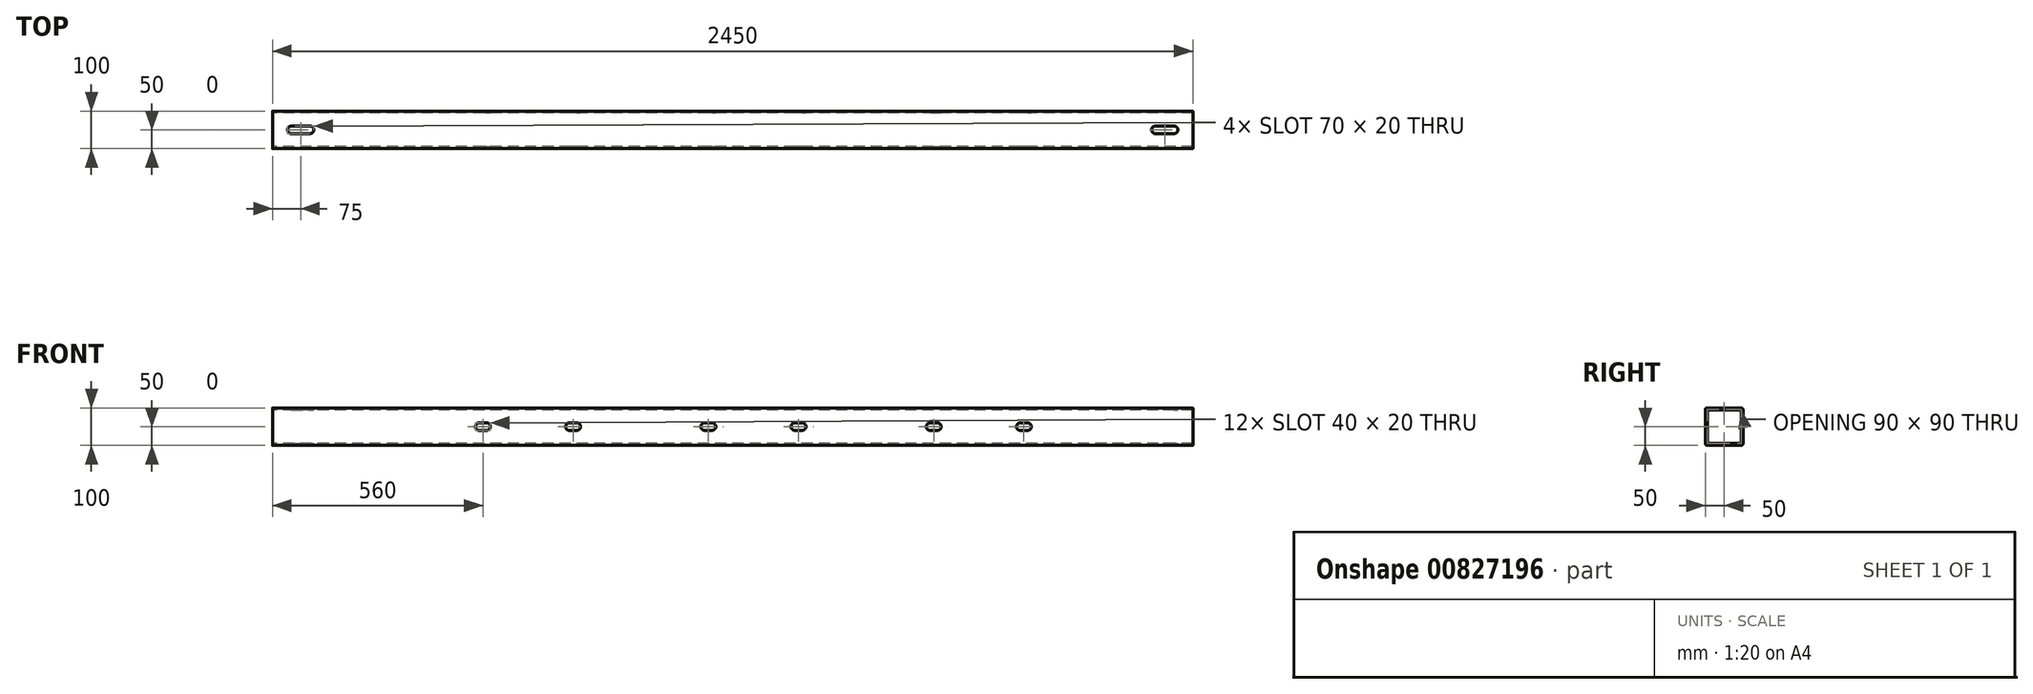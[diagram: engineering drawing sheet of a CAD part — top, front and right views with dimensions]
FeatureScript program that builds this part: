
annotation { "Feature Type Name" : "Feature", "Feature Type Description" : "" }
export const myFeature = defineFeature(function(context is Context, id is Id, definition is map)
    precondition{}
    {
        {
            var Q0;
            Q0=qCreatedBy(makeId("Right.planeOp"),FACE);
            var sketch = newSketch(context, id + "F0", { "sketchPlane" : qUnion([Q0])});
            skLineSegment(sketch, "E0.bottom", {"start": v(-45, 50) * mm, "end": v(45, 50) * mm});
            skLineSegment(sketch, "E0.top", {"start": v(-45, -50) * mm, "end": v(45, -50) * mm});
            skLineSegment(sketch, "E0.left", {"start": v(-50, 45) * mm, "end": v(-50, -45) * mm});
            skLineSegment(sketch, "E0.right", {"start": v(50, 45) * mm, "end": v(50, -45) * mm});
            skLineSegment(sketch, "E1.bottom", {"start": v(-41, 45) * mm, "end": v(41, 45) * mm});
            skLineSegment(sketch, "E1.top", {"start": v(-41, -45) * mm, "end": v(41, -45) * mm});
            skLineSegment(sketch, "E1.left", {"start": v(-45, 41) * mm, "end": v(-45, -41) * mm});
            skLineSegment(sketch, "E1.right", {"start": v(45, 41) * mm, "end": v(45, -41) * mm});
            skPoint(sketch, "E2.visualSharp", {"position": v(-45, 45) * mm});
            skArc(sketch, "E2.filletArc", {"start": v(-41, 45) * mm, "mid": v(-43.83, 43.83) * mm, "end": v(-45, 41) * mm});
            skPoint(sketch, "E3.visualSharp", {"position": v(-45, -45) * mm});
            skArc(sketch, "E3.filletArc", {"start": v(-45, -41) * mm, "mid": v(-43.83, -43.83) * mm, "end": v(-41, -45) * mm});
            skPoint(sketch, "E4.visualSharp", {"position": v(45, -45) * mm});
            skArc(sketch, "E4.filletArc", {"start": v(41, -45) * mm, "mid": v(43.83, -43.83) * mm, "end": v(45, -41) * mm});
            skPoint(sketch, "E5.visualSharp", {"position": v(45, 45) * mm});
            skArc(sketch, "E5.filletArc", {"start": v(45, 41) * mm, "mid": v(43.83, 43.83) * mm, "end": v(41, 45) * mm});
            skPoint(sketch, "E6.visualSharp", {"position": v(-50, 50) * mm});
            skArc(sketch, "E6.filletArc", {"start": v(-45, 50) * mm, "mid": v(-48.54, 48.54) * mm, "end": v(-50, 45) * mm});
            skPoint(sketch, "E7.visualSharp", {"position": v(-50, -50) * mm});
            skArc(sketch, "E7.filletArc", {"start": v(-50, -45) * mm, "mid": v(-48.54, -48.54) * mm, "end": v(-45, -50) * mm});
            skPoint(sketch, "E8.visualSharp", {"position": v(50, -50) * mm});
            skArc(sketch, "E8.filletArc", {"start": v(45, -50) * mm, "mid": v(48.54, -48.54) * mm, "end": v(50, -45) * mm});
            skPoint(sketch, "E9.visualSharp", {"position": v(50, 50) * mm});
            skArc(sketch, "E9.filletArc", {"start": v(50, 45) * mm, "mid": v(48.54, 48.54) * mm, "end": v(45, 50) * mm});
            skSolve(sketch);
        }
        {
            var Q0;
            Q0=makeQuery(id+"F0.imprint","IMPRINT",FACE,{"disambiguationData":[TD([[makeQuery(id+"F0.imprint","IMPRINT",EDGE,{"derivedFrom":sQuery(id+"F0.wireOp",EDGE,"E0.bottom")}),-1.0]])]});
            extrude(context, id + "F1", {"entities" : qUnion([Q0]), "endBound" : BoundingType.SYMMETRIC, "depth" : 2450 * mm, "offsetDistance" : 25 * mm});
        }
        {
            var Q0;
            Q0=makeQuery(id+"F1.opExtrude","SWEPT_FACE",FACE,{"disambiguationData":[OSD([sQuery(id+"F0.wireOp",EDGE,"E0.left")])]});
            var sketch = newSketch(context, id + "F2", { "sketchPlane" : qUnion([Q0])});
            skArc(sketch, "E10", {"start": v(-682.6, -6.5) * mm, "mid": v(-679.19, -9.08) * mm, "end": v(-675, -10) * mm});
            skArc(sketch, "E11", {"start": v(-655, -10) * mm, "mid": v(-645, 0) * mm, "end": v(-655, 10) * mm});
            skLineSegment(sketch, "E12", {"start": v(-675, -10) * mm, "end": v(-655, -10) * mm});
            skArc(sketch, "E13", {"start": v(-435, 10) * mm, "mid": v(-445, 0) * mm, "end": v(-435, -10) * mm});
            skArc(sketch, "E14", {"start": v(-425, 0) * mm, "mid": v(-407.93, -7.07) * mm, "end": v(-415, 10) * mm});
            skArc(sketch, "E15", {"start": v(-75, 10) * mm, "mid": v(-85, 0) * mm, "end": v(-75, -10) * mm});
            skArc(sketch, "E16", {"start": v(185, -10) * mm, "mid": v(195, 0) * mm, "end": v(185, 10) * mm});
            skArc(sketch, "E17", {"start": v(165, 10) * mm, "mid": v(155, 0) * mm, "end": v(165, -10) * mm});
            skArc(sketch, "E18", {"start": v(-55, -10) * mm, "mid": v(-45, 0) * mm, "end": v(-55, 10) * mm});
            skArc(sketch, "E19", {"start": v(525, 10) * mm, "mid": v(515, 0) * mm, "end": v(525, -10) * mm});
            skArc(sketch, "E20", {"start": v(545, -10) * mm, "mid": v(555, 0) * mm, "end": v(545, 10) * mm});
            skArc(sketch, "E21", {"start": v(765, 10) * mm, "mid": v(755, 0) * mm, "end": v(765, -10) * mm});
            skArc(sketch, "E22", {"start": v(785, -10) * mm, "mid": v(795, 0) * mm, "end": v(785, 10) * mm});
            skLineSegment(sketch, "E23", {"start": v(-435, 10) * mm, "end": v(-415, 10) * mm});
            skLineSegment(sketch, "E24", {"start": v(-435, -10) * mm, "end": v(-415, -10) * mm});
            skLineSegment(sketch, "E25", {"start": v(-75, 10) * mm, "end": v(-55, 10) * mm});
            skLineSegment(sketch, "E26", {"start": v(-55, -10) * mm, "end": v(-75, -10) * mm});
            skLineSegment(sketch, "E27", {"start": v(165, 10) * mm, "end": v(185, 10) * mm});
            skLineSegment(sketch, "E28", {"start": v(165, -10) * mm, "end": v(185, -10) * mm});
            skLineSegment(sketch, "E29", {"start": v(545, 10) * mm, "end": v(525, 10) * mm});
            skLineSegment(sketch, "E30", {"start": v(525, -10) * mm, "end": v(545, -10) * mm});
            skLineSegment(sketch, "E31", {"start": v(765, 10) * mm, "end": v(785, 10) * mm});
            skLineSegment(sketch, "E32", {"start": v(765, -10) * mm, "end": v(785, -10) * mm});
            skArc(sketch, "E33", {"start": v(-675, 10) * mm, "mid": v(-684.08, 4.19) * mm, "end": v(-682.6, -6.5) * mm});
            skLineSegment(sketch, "E34", {"start": v(-675, 10) * mm, "end": v(-655, 10) * mm});
            skSolve(sketch);
        }
        {
            var Q0;
            Q0 = qSketchRegion(id + "F2", true);
            extrude(context, id + "F3", {"entities" : qUnion([Q0]), "operationType" : NewBodyOperationType.REMOVE, "endBound" : BoundingType.THROUGH_ALL, "oppositeDirection" : true, "depth" : 25 * mm, "offsetDistance" : 25 * mm});
        }
        {
            var Q0;
            Q0=makeQuery(id+"F1.opExtrude","SWEPT_FACE",FACE,{"disambiguationData":[OSD([sQuery(id+"F0.wireOp",EDGE,"E0.bottom")])]});
            var sketch = newSketch(context, id + "F4", { "sketchPlane" : qUnion([Q0])});
            skArc(sketch, "E35", {"start": v(-1175, 10) * mm, "mid": v(-1185, 0) * mm, "end": v(-1175, -10) * mm});
            skArc(sketch, "E36", {"start": v(-1125, -10) * mm, "mid": v(-1115, 0) * mm, "end": v(-1125, 10) * mm});
            skLineSegment(sketch, "E37", {"start": v(-1175, 10) * mm, "end": v(-1125, 10) * mm});
            skLineSegment(sketch, "E38", {"start": v(-1175, -10) * mm, "end": v(-1125, -10) * mm});
            skLineSegment(sketch, "E39.MirrorCS", {"start": v(1175, 10) * mm, "end": v(1125, 10) * mm});
            skArc(sketch, "E40.MirrorCS", {"start": v(1175, 10) * mm, "mid": v(1185, 0) * mm, "end": v(1175, -10) * mm});
            skLineSegment(sketch, "E41.MirrorCS", {"start": v(1175, -10) * mm, "end": v(1125, -10) * mm});
            skArc(sketch, "E42.MirrorCS", {"start": v(1125, -10) * mm, "mid": v(1115, 0) * mm, "end": v(1125, 10) * mm});
            skSolve(sketch);
        }
        {
            var Q0;
            Q0 = qSketchRegion(id + "F4", true);
            extrude(context, id + "F5", {"entities" : qUnion([Q0]), "operationType" : NewBodyOperationType.REMOVE, "endBound" : BoundingType.THROUGH_ALL, "oppositeDirection" : true, "depth" : 25 * mm, "offsetDistance" : 25 * mm});
        }
    });
